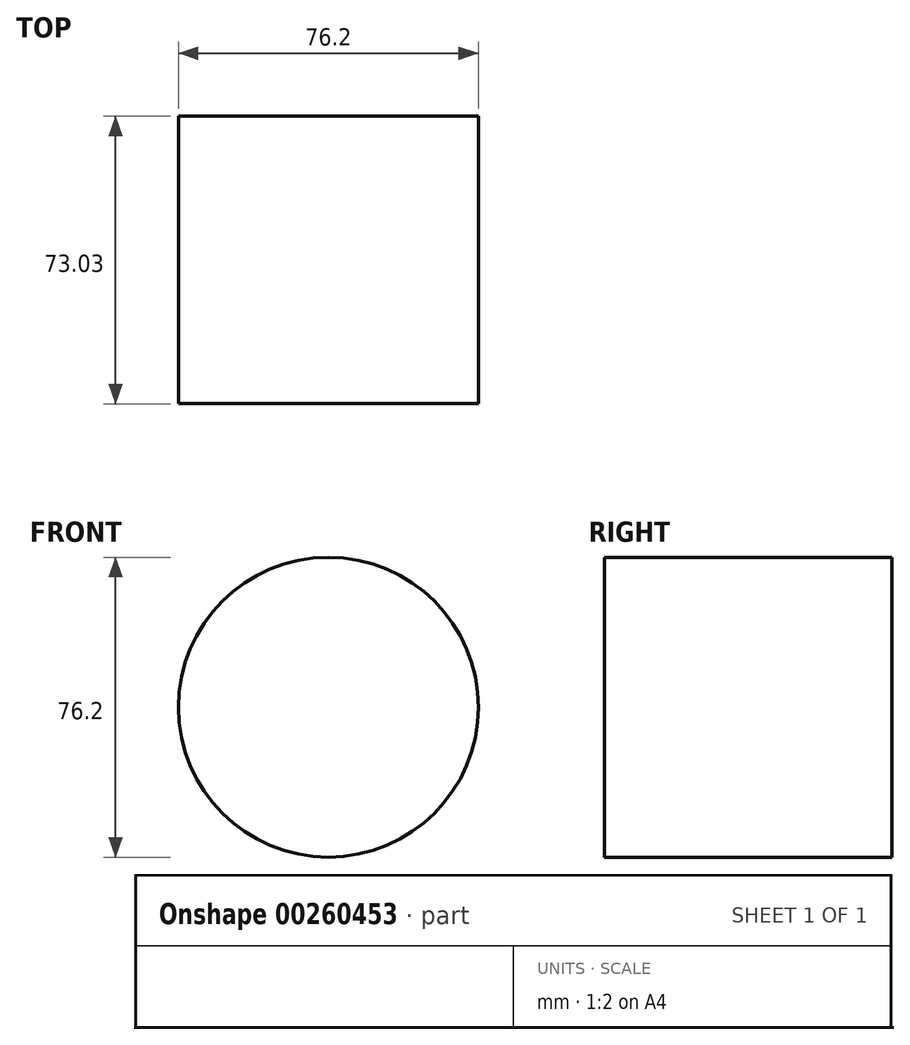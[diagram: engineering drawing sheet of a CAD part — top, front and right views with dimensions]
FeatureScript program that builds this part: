
annotation { "Feature Type Name" : "Feature", "Feature Type Description" : "" }
export const myFeature = defineFeature(function(context is Context, id is Id, definition is map)
    precondition{}
    {
        {
            var Q0;
            Q0=qCreatedBy(makeId("Front.planeOp"),FACE);
            var sketch = newSketch(context, id + "F0", { "sketchPlane" : qUnion([Q0])});
            skCircle(sketch, "E0", {"center": v(0, 0) * mm, "radius": 38.1 * mm});
            skSolve(sketch);
        }
        {
            var Q0;
            Q0 = qSketchRegion(id + "F0", true);
            extrude(context, id + "F1", {"entities" : qUnion([Q0]), "depth" : 73.02 * mm});
        }
    });
